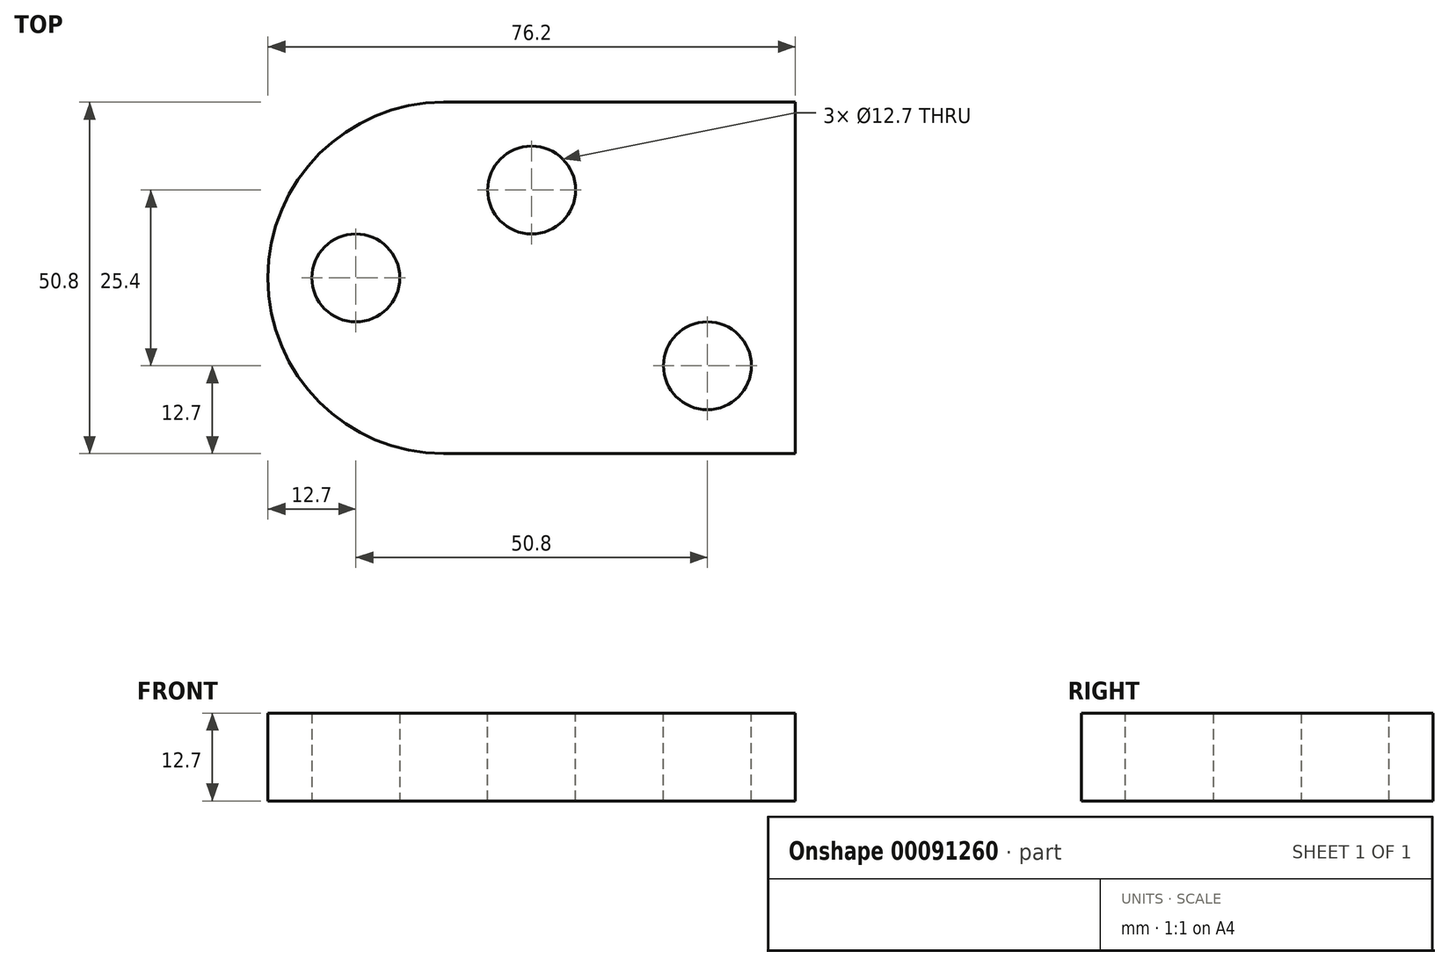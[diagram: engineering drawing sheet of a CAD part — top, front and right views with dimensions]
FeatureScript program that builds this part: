
annotation { "Feature Type Name" : "Feature", "Feature Type Description" : "" }
export const myFeature = defineFeature(function(context is Context, id is Id, definition is map)
    precondition{}
    {
        {
            var Q0;
            Q0=qCreatedBy(makeId("Top.planeOp"),FACE);
            var sketch = newSketch(context, id + "F0", { "sketchPlane" : qUnion([Q0])});
            skLineSegment(sketch, "E0.bottom", {"start": v(25.4, 25.4) * mm, "end": v(-25.4, 25.4) * mm});
            skLineSegment(sketch, "E0.top", {"start": v(25.4, -25.4) * mm, "end": v(-25.4, -25.4) * mm});
            skLineSegment(sketch, "E0.left", {"start": v(25.4, 25.4) * mm, "end": v(25.4, -25.4) * mm});
            skLineSegment(sketch, "E0.right", {"start": v(-25.4, 25.4) * mm, "end": v(-25.4, -25.4) * mm});
            skPoint(sketch, "E0.middle", {"position": v(0, 0) * mm});
            skArc(sketch, "E1", {"start": v(-25.4, 25.4) * mm, "mid": v(-50.8, 0) * mm, "end": v(-25.4, -25.4) * mm});
            skLineSegment(sketch, "E2", {"start": v(0, 0) * mm, "end": v(-25.4, 0) * mm, "construction": true});
            skLineSegment(sketch, "E3", {"start": v(0, 0) * mm, "end": v(0, -25.4) * mm, "construction": true});
            skLineSegment(sketch, "E4", {"start": v(-12.7, 0) * mm, "end": v(-12.7, -12.7) * mm, "construction": true});
            skPoint(sketch, "E4.endSnap0", {"position": v(0, -12.7) * mm});
            skLineSegment(sketch, "E5", {"start": v(-12.7, -12.7) * mm, "end": v(0, -12.7) * mm, "construction": true});
            skCircle(sketch, "E6", {"center": v(-12.7, -12.7) * mm, "radius": 6.35 * mm});
            skCircle(sketch, "E7.MirrorC", {"center": v(12.7, -12.7) * mm, "radius": 6.35 * mm});
            skCircle(sketch, "E8.MirrorC", {"center": v(-12.7, 12.7) * mm, "radius": 6.35 * mm});
            skCircle(sketch, "E9.MirrorC", {"center": v(12.7, 12.7) * mm, "radius": 6.35 * mm});
            skLineSegment(sketch, "E10", {"start": v(-25.4, 0) * mm, "end": v(-50.8, 0) * mm, "construction": true});
            skCircle(sketch, "E11", {"center": v(-38.1, 0) * mm, "radius": 6.35 * mm});
            skSolve(sketch);
        }
        {
            var Q0;
            Q0=makeQuery(id+"F0.imprint","IMPRINT",FACE,{"disambiguationData":[TD([[makeQuery(id+"F0.imprint","IMPRINT",EDGE,{"derivedFrom":sQuery(id+"F0.wireOp",EDGE,"E0.right")}),-1.0]])]});
            extrude(context, id + "F1", {"entities" : qUnion([Q0]), "depth" : 6.35 * mm, "hasSecondDirection" : true, "secondDirectionOppositeDirection" : true, "secondDirectionDepth" : 6.35 * mm});
        }
        {
            var Q0;
            Q0=makeQuery(id+"F0.imprint","IMPRINT",FACE,{"disambiguationData":[TD([[makeQuery(id+"F0.imprint","IMPRINT",EDGE,{"derivedFrom":sQuery(id+"F0.wireOp",EDGE,"E0.bottom")}),1.0]])]});
            extrude(context, id + "F2", {"entities" : qUnion([Q0]), "operationType" : NewBodyOperationType.ADD, "oppositeDirection" : true, "depth" : 6.35 * mm});
        }
        {
            var Q0;
            Q0=makeQuery(id+"F0.imprint","IMPRINT",FACE,{"disambiguationData":[TD([[makeQuery(id+"F0.imprint","IMPRINT",EDGE,{"derivedFrom":sQuery(id+"F0.wireOp",EDGE,"E0.bottom")}),1.0]])]});
            var Q1;
            Q1=makeQuery(id+"F0.imprint","IMPRINT",FACE,{"disambiguationData":[TD([[makeQuery(id+"F0.imprint","IMPRINT",EDGE,{"derivedFrom":sQuery(id+"F0.wireOp",EDGE,"E6")}),1.0]])]});
            var Q2;
            Q2=makeQuery(id+"F0.imprint","IMPRINT",FACE,{"disambiguationData":[TD([[makeQuery(id+"F0.imprint","IMPRINT",EDGE,{"derivedFrom":sQuery(id+"F0.wireOp",EDGE,"E7.MirrorC")}),-1.0]])]});
            var Q3;
            Q3=makeQuery(id+"F0.imprint","IMPRINT",FACE,{"disambiguationData":[TD([[makeQuery(id+"F0.imprint","IMPRINT",EDGE,{"derivedFrom":sQuery(id+"F0.wireOp",EDGE,"E9.MirrorC")}),1.0]])]});
            var Q4;
            Q4=makeQuery(id+"F0.imprint","IMPRINT",FACE,{"disambiguationData":[TD([[makeQuery(id+"F0.imprint","IMPRINT",EDGE,{"derivedFrom":sQuery(id+"F0.wireOp",EDGE,"E8.MirrorC")}),-1.0]])]});
            extrude(context, id + "F3", {"entities" : qUnion([Q0, Q1, Q2, Q3, Q4]), "depth" : 6.35 * mm});
        }
        {
            var Q0;
            Q0=makeQuery(id+"F0.imprint","IMPRINT",FACE,{"disambiguationData":[TD([[makeQuery(id+"F0.imprint","IMPRINT",EDGE,{"derivedFrom":sQuery(id+"F0.wireOp",EDGE,"E7.MirrorC")}),-1.0]])]});
            var Q1;
            Q1=makeQuery(id+"F0.imprint","IMPRINT",FACE,{"disambiguationData":[TD([[makeQuery(id+"F0.imprint","IMPRINT",EDGE,{"derivedFrom":sQuery(id+"F0.wireOp",EDGE,"E9.MirrorC")}),1.0]])]});
            var Q2;
            Q2=makeQuery(id+"F0.imprint","IMPRINT",FACE,{"disambiguationData":[TD([[makeQuery(id+"F0.imprint","IMPRINT",EDGE,{"derivedFrom":sQuery(id+"F0.wireOp",EDGE,"E8.MirrorC")}),-1.0]])]});
            var Q3;
            Q3=makeQuery(id+"F0.imprint","IMPRINT",FACE,{"disambiguationData":[TD([[makeQuery(id+"F0.imprint","IMPRINT",EDGE,{"derivedFrom":sQuery(id+"F0.wireOp",EDGE,"E6")}),1.0]])]});
            extrude(context, id + "F4", {"entities" : qUnion([Q0, Q1, Q2, Q3]), "operationType" : NewBodyOperationType.ADD, "oppositeDirection" : true, "depth" : 6.35 * mm});
        }
    });
